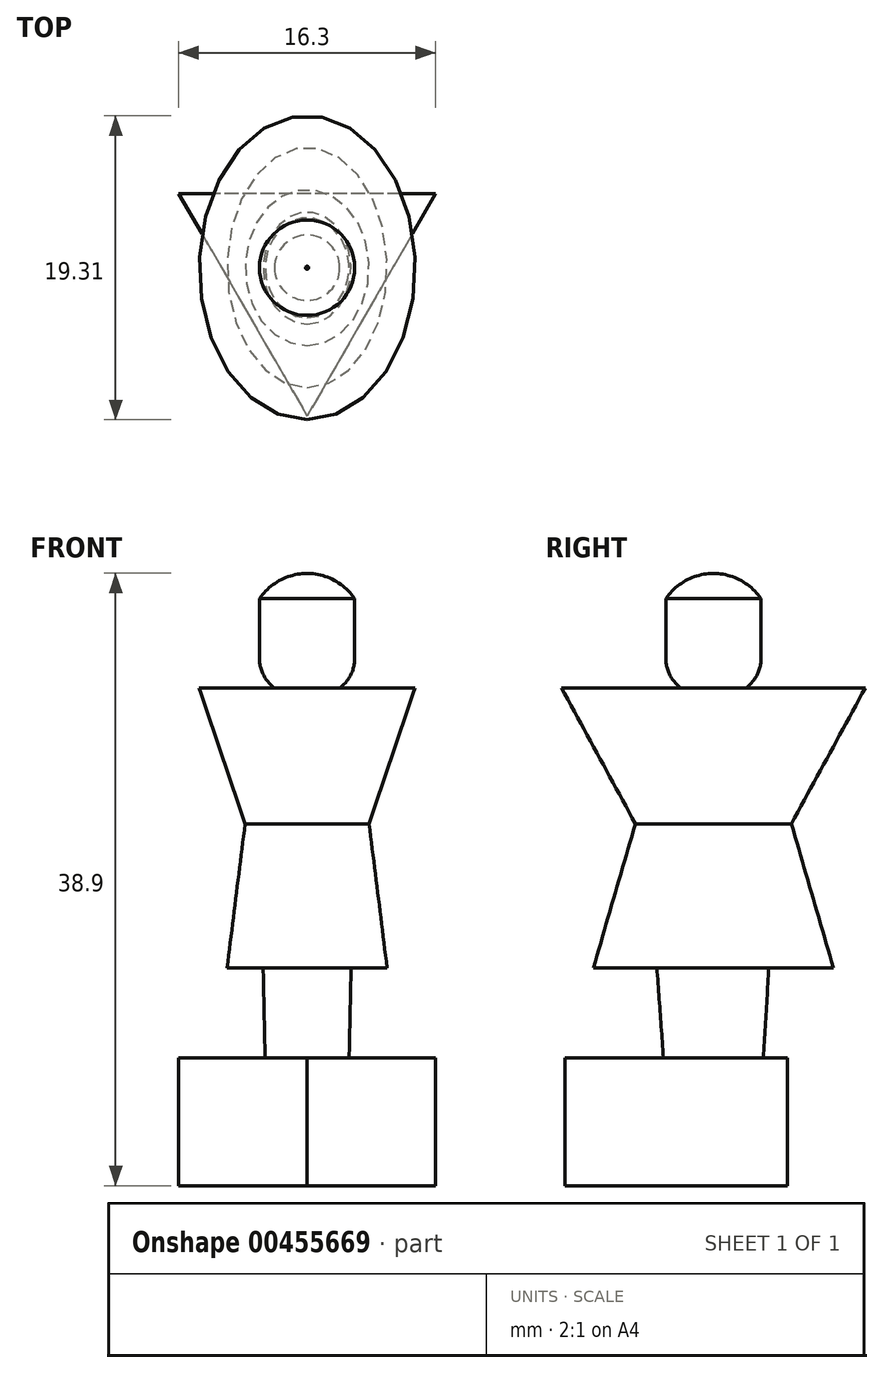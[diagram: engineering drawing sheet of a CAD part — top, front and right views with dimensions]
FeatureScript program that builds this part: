
annotation { "Feature Type Name" : "Feature", "Feature Type Description" : "" }
export const myFeature = defineFeature(function(context is Context, id is Id, definition is map)
    precondition{}
    {
        {
            var Q0;
            Q0=qCreatedBy(makeId("Top.planeOp"),FACE);
            var sketch = newSketch(context, id + "F0", { "sketchPlane" : qUnion([Q0])});
            skLineSegment(sketch, "E0", {"start": v(8.15, 14.12) * mm, "end": v(-8.15, 14.12) * mm});
            skLineSegment(sketch, "E1", {"start": v(8.15, 14.12) * mm, "end": v(0, 0) * mm});
            skLineSegment(sketch, "E2", {"start": v(-8.15, 14.12) * mm, "end": v(0, 0) * mm});
            skSolve(sketch);
        }
        {
            var Q0;
            Q0=makeQuery(id+"F0.imprint","IMPRINT",FACE,{"disambiguationData":[TD([[makeQuery(id+"F0.imprint","IMPRINT",EDGE,{"derivedFrom":sQuery(id+"F0.wireOp",EDGE,"E0")}),1.0]])]});
            extrude(context, id + "F1", {"entities" : qUnion([Q0]), "depth" : 8.13 * mm});
        }
        {
            var Q0;
            Q0=makeQuery(id+"F1.opExtrude","CAP_FACE",FACE,{"disambiguationData":[OSD([sQuery(id+"F0.wireOp",EDGE,"E0"),sQuery(id+"F0.wireOp",EDGE,"E1"),sQuery(id+"F0.wireOp",EDGE,"E2")])],"isStart":false});
            var sketch = newSketch(context, id + "F2", { "sketchPlane" : qUnion([Q0])});
            skEllipse(sketch, "E3", {"center": v(0, 9.41) * mm, "majorRadius": 3.18 * mm, "minorRadius": 2.67 * mm, "majorAxis": v(0, -1)});
            skSolve(sketch);
        }
        {
            var Q0;
            {var subQ0=makeQuery(id+"F1.opExtrude","CAP_EDGE",EDGE,{"disambiguationData":[OSD([sQuery(id+"F0.wireOp",EDGE,"E0")])],"isStart":false});Q0=makeQuery(id+"F2.imprint","IMPRINT",FACE,{"disambiguationData":[TD([[makeQuery(id+"F2.imprint","IMPRINT",EDGE,{"derivedFrom":subQ0}),1.0]])]});}
            cPlane(context, id + "F3", {"entities" : qUnion([Q0]), "cplaneType" : CPlaneType.OFFSET, "offset" : 5.7 * mm, "width" : 152.4 * mm, "height" : 152.4 * mm});
        }
        {
            var Q0;
            Q0=qCreatedBy(id+"F3.planeOp",FACE);
            var sketch = newSketch(context, id + "F4", { "sketchPlane" : qUnion([Q0])});
            skPoint(sketch, "E4.endSnap0", {"position": v(4.1, 7.05) * mm});
            skEllipse(sketch, "E5", {"center": v(0, 9.38) * mm, "majorRadius": 3.56 * mm, "minorRadius": 2.8 * mm, "majorAxis": v(0, 1)});
            skSolve(sketch);
        }
        {
            var Q1;
            Q1 = qSketchRegion(id + "F2", true);
            var Q2;
            Q2 = qSketchRegion(id + "F4", true);
            loft(context, id + "F5", {"operationType" : NewBodyOperationType.ADD, "sheetProfilesArray" : [{ "sheetProfileEntities" : qUnion([Q1]) }, { "sheetProfileEntities" : qUnion([Q2]) }]});
        }
        {
            var Q0;
            Q0=qCreatedBy(id+"F3.planeOp",FACE);
            cPlane(context, id + "F6", {"entities" : qUnion([Q0]), "cplaneType" : CPlaneType.OFFSET, "offset" : 9.14 * mm, "width" : 152.4 * mm, "height" : 152.4 * mm});
        }
        {
            var Q0;
            Q0=qCreatedBy(id+"F6.planeOp",FACE);
            cPlane(context, id + "F7", {"entities" : qUnion([Q0]), "cplaneType" : CPlaneType.OFFSET, "offset" : 8.64 * mm, "width" : 152.4 * mm, "height" : 152.4 * mm});
        }
        {
            var Q0;
            Q0=qCreatedBy(makeId("Front.planeOp"),FACE);
            cPlane(context, id + "F8", {"entities" : qUnion([Q0]), "cplaneType" : CPlaneType.OFFSET, "offset" : 9.4 * mm, "oppositeDirection" : true, "width" : 152.4 * mm, "height" : 152.4 * mm});
        }
        {
            var Q0;
            Q0=qCreatedBy(id+"F3.planeOp",FACE);
            var sketch = newSketch(context, id + "F9", { "sketchPlane" : qUnion([Q0])});
            skEllipse(sketch, "E6", {"center": v(0, 9.42) * mm, "majorRadius": 7.62 * mm, "minorRadius": 5.08 * mm, "majorAxis": v(0, -1)});
            skSolve(sketch);
        }
        {
            var Q0;
            Q0=qCreatedBy(id+"F6.planeOp",FACE);
            var sketch = newSketch(context, id + "F10", { "sketchPlane" : qUnion([Q0])});
            skEllipse(sketch, "E7", {"center": v(0, 9.41) * mm, "majorRadius": 4.95 * mm, "minorRadius": 3.94 * mm, "majorAxis": v(0, -1)});
            skSolve(sketch);
        }
        {
            var Q0;
            Q0=qCreatedBy(id+"F7.planeOp",FACE);
            var sketch = newSketch(context, id + "F11", { "sketchPlane" : qUnion([Q0])});
            skEllipse(sketch, "E8", {"center": v(0, 9.41) * mm, "majorRadius": 9.65 * mm, "minorRadius": 6.86 * mm, "majorAxis": v(0, -1)});
            skSolve(sketch);
        }
        {
            var Q1;
            Q1=makeQuery(id+"F9.imprint","IMPRINT",FACE,{"disambiguationData":[TD([[makeQuery(id+"F9.imprint","IMPRINT",EDGE,{"derivedFrom":sQuery(id+"F9.wireOp",EDGE,"E6")}),1.0]])]});
            var Q2;
            Q2=makeQuery(id+"F10.imprint","IMPRINT",FACE,{"disambiguationData":[TD([[makeQuery(id+"F10.imprint","IMPRINT",EDGE,{"derivedFrom":sQuery(id+"F10.wireOp",EDGE,"E7")}),1.0]])]});
            loft(context, id + "F12", {"operationType" : NewBodyOperationType.ADD, "sheetProfilesArray" : [{ "sheetProfileEntities" : qUnion([Q1]) }, { "sheetProfileEntities" : qUnion([Q2]) }]});
        }
        {
            var Q1;
            Q1=makeQuery(id+"F12.opLoft","CAP_FACE",FACE,{"disambiguationData":[OSD([makeQuery(id+"F10.imprint","IMPRINT",FACE,{"disambiguationData":[TD([[makeQuery(id+"F10.imprint","IMPRINT",EDGE,{"derivedFrom":sQuery(id+"F10.wireOp",EDGE,"E7")}),1.0]])]})])],"isStart":true});
            var Q2;
            Q2=makeQuery(id+"F11.imprint","IMPRINT",FACE,{"disambiguationData":[TD([[makeQuery(id+"F11.imprint","IMPRINT",EDGE,{"derivedFrom":sQuery(id+"F11.wireOp",EDGE,"E8")}),1.0]])]});
            loft(context, id + "F13", {"operationType" : NewBodyOperationType.ADD, "sheetProfilesArray" : [{ "sheetProfileEntities" : qUnion([Q1]) }, { "sheetProfileEntities" : qUnion([Q2]) }]});
        }
        {
            var Q0;
            Q0=qCreatedBy(id+"F8.planeOp",FACE);
            var sketch = newSketch(context, id + "F14", { "sketchPlane" : qUnion([Q0])});
            skLineSegment(sketch, "E9", {"start": v(0, 31.3) * mm, "end": v(0, 38.9) * mm});
            skArc(sketch, "E10", {"start": v(3.02, 37.29) * mm, "mid": v(1.7, 38.46) * mm, "end": v(0, 38.9) * mm});
            skLineSegment(sketch, "E11", {"start": v(3.02, 37.29) * mm, "end": v(3.02, 33.5) * mm});
            skArc(sketch, "E12", {"start": v(0, 31.3) * mm, "mid": v(2.07, 31.62) * mm, "end": v(3.02, 33.5) * mm});
            skSolve(sketch);
        }
        {
            var Q0;
            Q0=makeQuery(id+"F14.imprint","IMPRINT",FACE,{"disambiguationData":[TD([[makeQuery(id+"F14.imprint","IMPRINT",EDGE,{"derivedFrom":sQuery(id+"F14.wireOp",EDGE,"E9")}),-1.0]])]});
            var Q1;
            Q1=sQuery(id+"F14.wireOp",EDGE,"E9");
            revolve(context, id + "F15", {"operationType" : NewBodyOperationType.ADD, "entities" : qUnion([Q0]), "axis" : qUnion([Q1]), "revolveType" : RevolveType.FULL});
        }
    });
